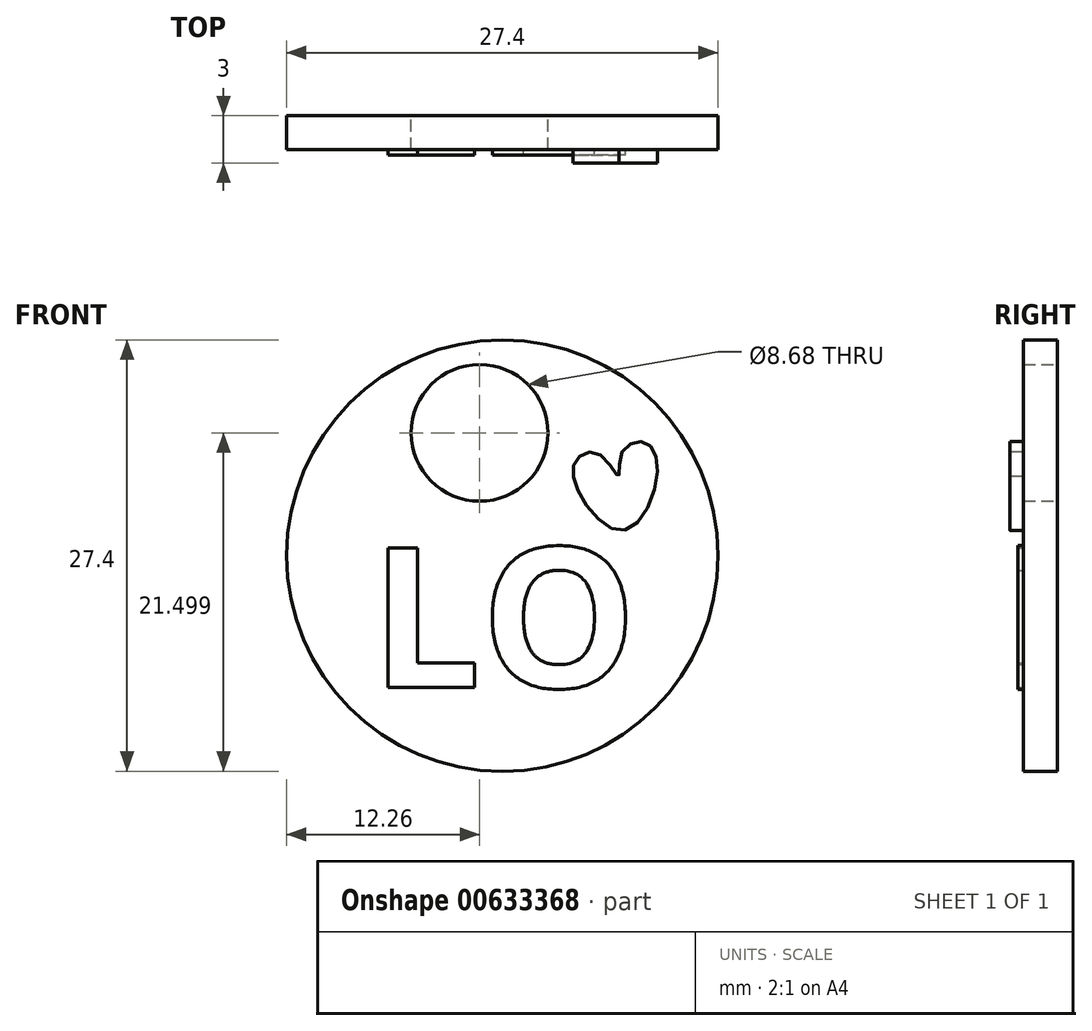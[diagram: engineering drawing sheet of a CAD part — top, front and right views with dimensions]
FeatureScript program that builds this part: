
annotation { "Feature Type Name" : "Feature", "Feature Type Description" : "" }
export const myFeature = defineFeature(function(context is Context, id is Id, definition is map)
    precondition{}
    {
        {
            var Q0;
            Q0=qCreatedBy(makeId("Front.planeOp"),FACE);
            var sketch = newSketch(context, id + "F0", { "sketchPlane" : qUnion([Q0])});
            skCircle(sketch, "E0", {"center": v(-33.5, 26.14) * mm, "radius": 13.7 * mm});
            skSolve(sketch);
        }
        {
            var Q0;
            Q0 = qSketchRegion(id + "F0", true);
            extrude(context, id + "F1", {"entities" : qUnion([Q0]), "depth" : 2.15 * mm, "offsetDistance" : 25.4 * mm});
        }
        {
            var Q0;
            Q0=qCreatedBy(makeId("Front.planeOp"),FACE);
            var sketch = newSketch(context, id + "F2", { "sketchPlane" : qUnion([Q0])});
            skCircle(sketch, "E1", {"center": v(-34.95, 33.94) * mm, "radius": 4.34 * mm});
            skSolve(sketch);
        }
        {
            var Q0;
            Q0 = qSketchRegion(id + "F2", true);
            extrude(context, id + "F3", {"entities" : qUnion([Q0]), "operationType" : NewBodyOperationType.REMOVE, "endBound" : BoundingType.UP_TO_NEXT, "depth" : 25.4 * mm, "offsetDistance" : 25.4 * mm});
        }
        {
            var Q0;
            Q0=qCreatedBy(makeId("Front.planeOp"),FACE);
            var sketch = newSketch(context, id + "F4", { "sketchPlane" : qUnion([Q0])});
            skText(sketch, "E2", { "text": "LO\n", "fontName": "OpenSans-Bold.ttf"});
            const initialGuessF4  = {"E2": [-0.04188, 0.01776, 1, 0, 0.00895]};
            skSetInitialGuess(sketch, initialGuessF4);
            skSolve(sketch);
        }
        {
            var Q0;
            Q0 = qSketchRegion(id + "F4", true);
            extrude(context, id + "F5", {"entities" : qUnion([Q0]), "operationType" : NewBodyOperationType.ADD, "depth" : 2.5 * mm, "offsetDistance" : 25.4 * mm});
        }
        {
            var Q0;
            Q0=qCreatedBy(makeId("Front.planeOp"),FACE);
            var sketch = newSketch(context, id + "F6", { "sketchPlane" : qUnion([Q0])});
            skFitSpline(sketch, "E3", {"points": [v(-25.7, 27.76) * mm, v(-28.53, 29.92) * mm, v(-28.83, 32.2) * mm, v(-27.33, 32.56) * mm, v(-26.12, 31.18) * mm, v(-25.94, 32.62) * mm, v(-24.5, 33.34) * mm, v(-23.66, 31.42) * mm, v(-25.7, 27.76) * mm]});
            skSolve(sketch);
        }
        {
            var Q0;
            Q0 = qSketchRegion(id + "F6", true);
            extrude(context, id + "F7", {"entities" : qUnion([Q0]), "operationType" : NewBodyOperationType.ADD, "depth" : 3 * mm, "offsetDistance" : 25.4 * mm});
        }
    });
